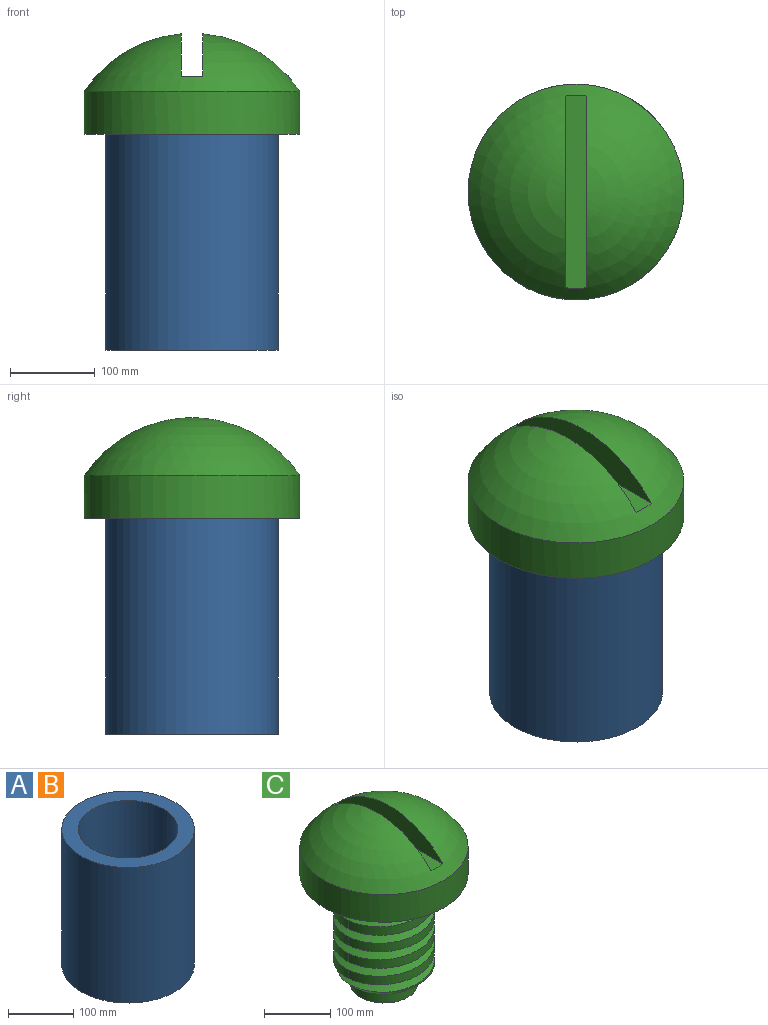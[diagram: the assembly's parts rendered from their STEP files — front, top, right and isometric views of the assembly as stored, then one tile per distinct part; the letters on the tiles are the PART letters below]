
ASSEMBLY  parts=3 mates=1
PART A: 4 faces, bbox 203.2x203.2x254 mm
  f0: cylinder r=76.2mm len=254mm, axis (0,0,-1), area 121609.8mm2, adj f2,f3
  f1: cylinder r=101.6mm len=254mm, axis (0,0,-1), area 162146.4mm2, adj f2,f3
  f2: plane 203.2x203.2mm, normal (0,0,1), area 14187.8mm2, adj f0,f1
  f3: plane 203.2x203.2mm, normal (0,0,-1), area 14187.8mm2, adj f0,f1
PART B: same geometry as A
PART C: 18 faces, bbox 254x254x321.8 mm
  f0: sphere r=152.4mm, area 58760.6mm2, adj f10,f11,f12,f13
  f1: plane 101.6x101.6mm, normal (0,0,-1), area 8107.3mm2, adj f2
  f2: cylinder r=50.8mm len=101.6mm, axis (0,0,-1), area 8107.3mm2, adj f1,f3
  f3: plane 127x127mm, normal (0,0,-1), area 4560.4mm2, adj f2,f17
  f4: cylinder r=76.2mm len=152.4mm, axis (0,0,-1), area 19731.1mm2, adj f5,f9,f14,f15,f16
  f5: cylinder r=76.2mm len=152.4mm, axis (0,0,-1), area 7571.6mm2, adj f4,f6,f15,f16
  f6: cylinder r=76.2mm len=152.4mm, axis (0,0,-1), area 7571.3mm2, adj f5,f7,f15,f16
  f7: cylinder r=76.2mm len=152.4mm, axis (0,0,-1), area 7571.2mm2, adj f6,f8,f15,f16
  f8: cylinder r=76.2mm len=152.4mm, axis (0,0,-1), area 4417mm2, adj f7,f15,f16,f17
  f9: plane 254x254mm, normal (0,0,-1), area 32429.3mm2, adj f4,f10
  f10: cylinder r=127mm len=254mm, axis (0,0,-1), area 40536.6mm2, adj f0,f9
  f11: plane 225.76x50.27mm, normal (1,0,0), area 7858.1mm2, adj f0,f12
  f12: plane 227.18x25.4mm, normal (0,0,1), area 5758.4mm2, adj f0,f11,f13
  f13: plane 225.76x50.27mm, normal (-1,0,0), area 7858.1mm2, adj f0,f12
  f14: plane 14.66x12.7mm, normal (0,-1,0), area 93.1mm2, adj f4,f15,f16
  f15: bspline ~179.79x170.99mm, area 30093.9mm2, adj f4,f5,f6,f7,f8,f14,f16,f17
  f16: bspline ~179.79x170.99mm, area 31647mm2, adj f4,f5,f6,f7,f8,f14,f15,f17
  f17: cone r=63.5mm half-angle=45deg, axis (0,0,1), area 5928mm2, adj f3,f8,f15,f16
PLACE A at identity
PLACE B at identity
PLACE C t=(0,0,50.8)mm
MATE planar C.f2 <-> B.f0  axis (0,0,-1) through (0,0,254)mm
